# Revit family: Shower-Valve_Trim-KALLISTA-One-P32360
name_source: partatom
category: Specialty Equipment
units: mm (PartAtom-declared; Revit-internal decimal feet)

## family parameters
Cut with Voids When Loaded = No
Host = Face
OmniClass Number = 23.31.25.00
OmniClass Title = Toilet and Bath Specialties
Part Type = Normal
Room Calculation Point = No
Round Connector Dimension = Use Diameter
Shared = No

## types (2) — shared parameters
ADA Compliant = No
Assembly Code = C1030200
Date Modified = 02/09/2023
Default Elevation = 42"
Description = Grand Lux, Volume Control
Handle Clearance = 2 13/16"
Height = 3 3/4"
Length = 3 3/4"
Manufacturer = Kallista Co.
Master Format 2014 = 10 28 00
Master Format 2014 Name = Toilet, Bath, and Laundry Accessories
Material = Premium Metal Construction
Product Name = One
URL = https://www.kallista.com
WaterSense Certified = No
Width = 3 3/4"

## per-type parameters (varying)
| type | Finish | Model | Secondary Finish | Type |
| BAF-Brushed French Gold | Kallista-Metal-BAF-Brushed_French_Gold | P32360-AD | Kallista-Metal-AD-Nickel_Silver | 1 |
| SN-Polished Nickel | Kallista-Metal-SN-Polished_Nickel | P32360-ULB | Kallista-Metal-ULB-Unlacquered_Brass | 2 |

## geometry (parser evidence)
native form markers: Sweep x6
no freeform markers — native parametric forms only
